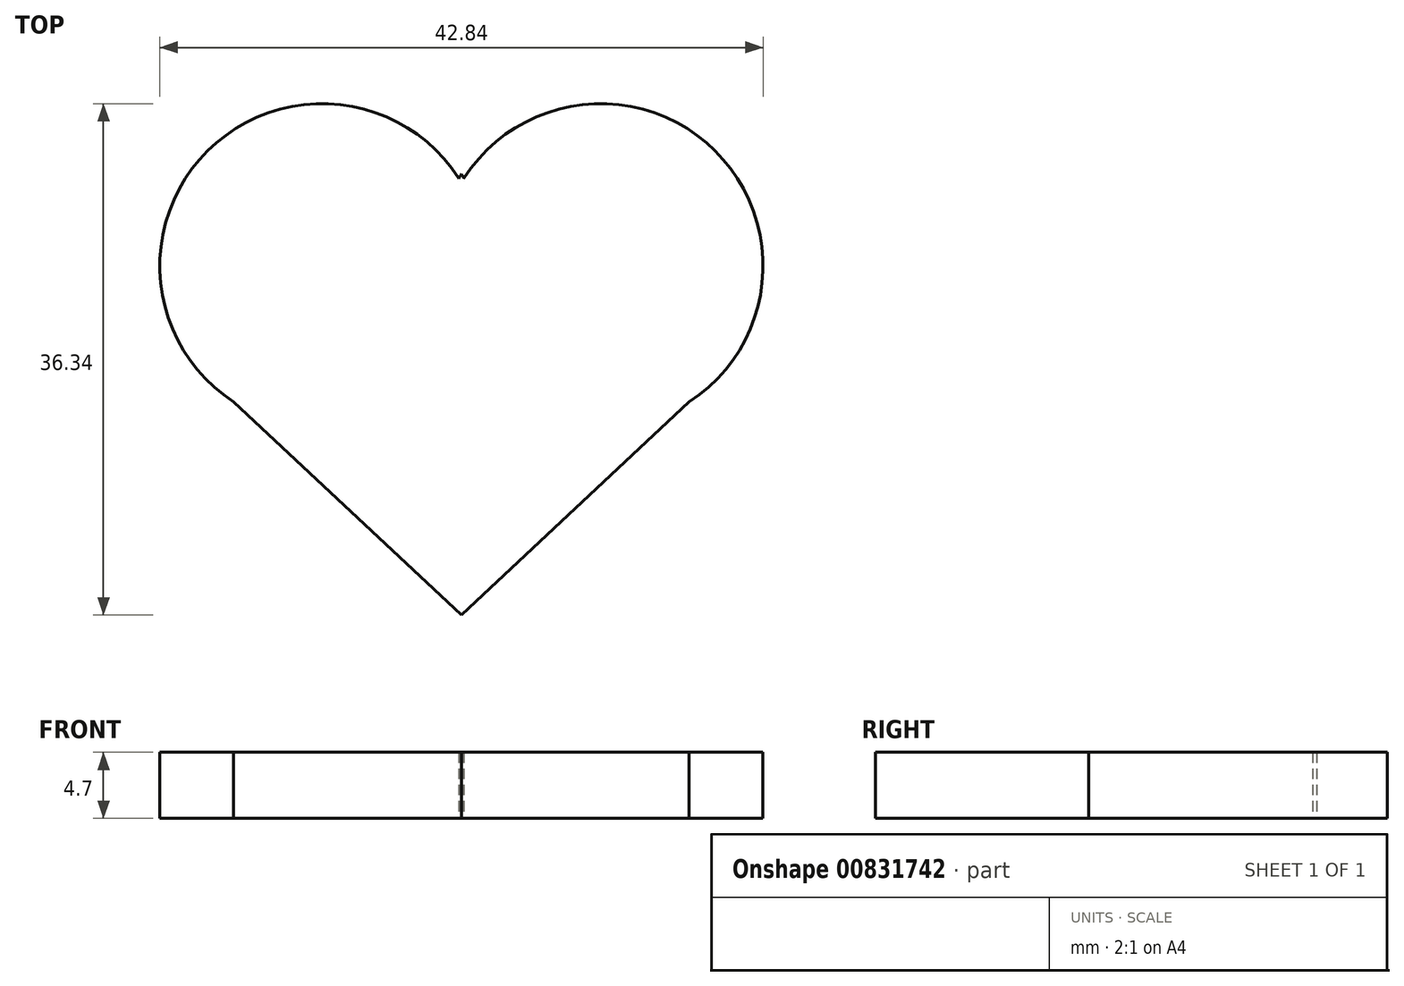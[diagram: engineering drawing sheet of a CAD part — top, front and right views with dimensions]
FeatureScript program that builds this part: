
annotation { "Feature Type Name" : "Feature", "Feature Type Description" : "" }
export const myFeature = defineFeature(function(context is Context, id is Id, definition is map)
    precondition{}
    {
        {
            var Q0;
            Q0=qCreatedBy(makeId("Top.planeOp"),FACE);
            var sketch = newSketch(context, id + "F0", { "sketchPlane" : qUnion([Q0])});
            skArc(sketch, "E0", {"start": v(-0.43, 10.24) * mm, "mid": v(-18.31, 12.49) * mm, "end": v(-16.56, -5.45) * mm});
            skArc(sketch, "E1.1.0", {"start": v(15.85, -4.94) * mm, "mid": v(17.27, 13.02) * mm, "end": v(-0.56, 10.45) * mm});
            skPoint(sketch, "E1.center", {"position": v(-10.27, -15.7) * mm});
            skFitSpline(sketch, "E2", {"points": [v(-16.56, -5.45) * mm, v(-0.38, -20.6) * mm], "startDerivative": vector(16.18, -15.15) * mm, "endDerivative": vector(16.18, -15.15) * mm});
            skFitSpline(sketch, "E3", {"points": [v(15.85, -5.2) * mm, v(-0.38, -20.6) * mm], "startDerivative": vector(-16.21, -15.44) * mm, "endDerivative": vector(-16.21, -15.44) * mm});
            skArc(sketch, "E4.MirrorCS", {"start": v(-16.62, -4.94) * mm, "mid": v(-18.04, 13.02) * mm, "end": v(-0.2, 10.45) * mm});
            skFitSpline(sketch, "E5.MirrorCS", {"points": [v(15.8, -5.45) * mm, v(-0.38, -20.6) * mm], "startDerivative": vector(-16.18, -15.15) * mm, "endDerivative": vector(-16.18, -15.15) * mm});
            skArc(sketch, "E6.MirrorCS", {"start": v(-0.34, 10.24) * mm, "mid": v(17.54, 12.49) * mm, "end": v(15.8, -5.45) * mm});
            skSolve(sketch);
        }
        {
            var Q0;
            {var subQ5=sQuery(id+"F0.wireOp",EDGE,"E2");Q0=makeQuery(id+"F0.imprint","IMPRINT",FACE,{"disambiguationData":[TD([[makeQuery(id+"F0.imprint","IMPRINT",EDGE,{"derivedFrom":subQ5}),1.0]])]});}
            extrude(context, id + "F1", {"entities" : qUnion([Q0]), "depth" : 4.7 * mm, "offsetDistance" : 25 * mm});
        }
    });
